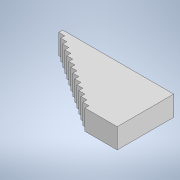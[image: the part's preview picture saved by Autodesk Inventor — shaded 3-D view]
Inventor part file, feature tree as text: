
AUTODESK INVENTOR PART (.ipt)
format: ipt  version: 2021 (Build 250183000, 183)  size: 149,504 bytes
history: native  units: mm
features: extrude x2, sketch x2, other x1
ambient origin geometry x8: Origin, YZ Plane, XZ Plane, XY Plane, X Axis, Y Axis, Z Axis, Center Point
bodies: Body1 (feature_tree)
feature tree (5):
  other  "ソリッド1"
  extrude  "押し出し1"  Depth=2800.0mm TaperAngle=0.0deg
  extrude  "押し出し6"  Depth=5500.0mm
  sketch  "スケッチ1"
  sketch  "スケッチ6"
